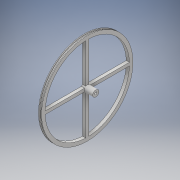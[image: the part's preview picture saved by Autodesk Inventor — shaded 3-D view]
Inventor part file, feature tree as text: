
AUTODESK INVENTOR PART (.ipt)
format: ipt  version: 2018 (Build 220112000, 112)  size: 169,472 bytes
history: native  units: mm
features: extrude x7, sketch x7, pattern_circular x1
ambient origin geometry x8: Origin, YZ Plane, XZ Plane, XY Plane, X Axis, Y Axis, Z Axis, Center Point
bodies: Solid1 (feature_tree)
feature tree (15):
  extrude  "Extrusion1"  Depth=2.0mm TaperAngle=0.0deg
  extrude  "Extrusion2"  Depth=1.0mm TaperAngle=0.0deg
  extrude  "Extrusion3"  Depth=1.0mm
  extrude  "Extrusion4"  Depth=3.0mm
  extrude  "Extrusion5"  Depth=5.0mm TaperAngle=0.0deg
  extrude  "Extrusion6"  Depth=4.0mm
  pattern_circular  "Circular Pattern1"  Count=4 Angle=360.0deg
  extrude  "Extrusion7"  Depth=15.0mm
  sketch  "Sketch1"  dims[d0=115.0mm d1=2.0mm d2=0.0mm]
  sketch  "Sketch2"  dims[d3=117.0mm d4=1.0mm d5=0.0mm]
  sketch  "Sketch3"  dims[d6=1.0mm d7=0.0mm d8=108.0mm]
  sketch  "Sketch4"  dims[d9=5.0mm d10=0.0mm d11=3.0mm]
  sketch  "Sketch5"  dims[d12=7.0mm d13=5.0mm d14=0.0mm]
  sketch  "Sketch6"  dims[d15=2.0mm d16=4.0mm]
  sketch  "Sketch7"  dims[d17=4.0mm d18=0.0mm d19=40.0mm d20=360.0deg d22=8.0mm d23=15.0mm d24=0.0mm]
